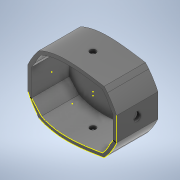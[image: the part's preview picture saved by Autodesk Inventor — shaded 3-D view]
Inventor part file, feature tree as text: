
AUTODESK INVENTOR PART (.ipt)
format: ipt  version: 2021.1 (Build 251245010, 245A)  size: 246,784 bytes
history: native  units: mm
features: sketch x6, extrude x6, plane x4, mirror x1
ambient origin geometry x8: Origin, YZ Plane, XZ Plane, XY Plane, X Axis, Y Axis, Z Axis, Center Point
bodies: Solid1 (feature_tree)
feature tree (17):
  sketch  "Sketch1"  dims[d1=70.0mm d2=70.0mm]
  sketch  "Sketch2"  dims[d3=0.0mm d4=6.0mm]
  extrude  "Extrusion1"  Depth=70.0mm
  extrude  "Extrusion2"  Depth=6.0mm
  plane  "Work Plane1"
  extrude  "Extrusion3"  TaperAngle=0.0deg  [1 undecoded]
  plane  "Work Plane2"
  sketch  "Sketch5"  dims[d5=64.0mm d6=0.0mm]
  mirror  "Mirror1"
  plane  "Work Plane3"
  extrude  "Extrusion4"  Depth=60.0mm TaperAngle=0.0deg
  plane  "Work Plane4"
  sketch  "Sketch6"  dims[d7=60.0mm d9=30.0mm d10=0.0mm]
  extrude  "Extrusion5"  Depth=49.152mm
  extrude  "Extrusion6"  Depth=10.0mm
  sketch  "Sketch7"  dims[d11=49.151954mm d12=49.152mm]
  sketch  "Sketch8"  dims[d13=10.0mm d14=10.0mm d15=20.0mm d16=0.0mm d19=40.0mm d20=6.0mm d21=6.0mm d22=35.0mm d23=15.0mm d24=0.0mm d28=0.0mm]
note: 1 required parameter value undecoded (feature->parameter linkage not recoverable at this tier; creation-order binding heuristic only, values carry confidence <= 0.55)
